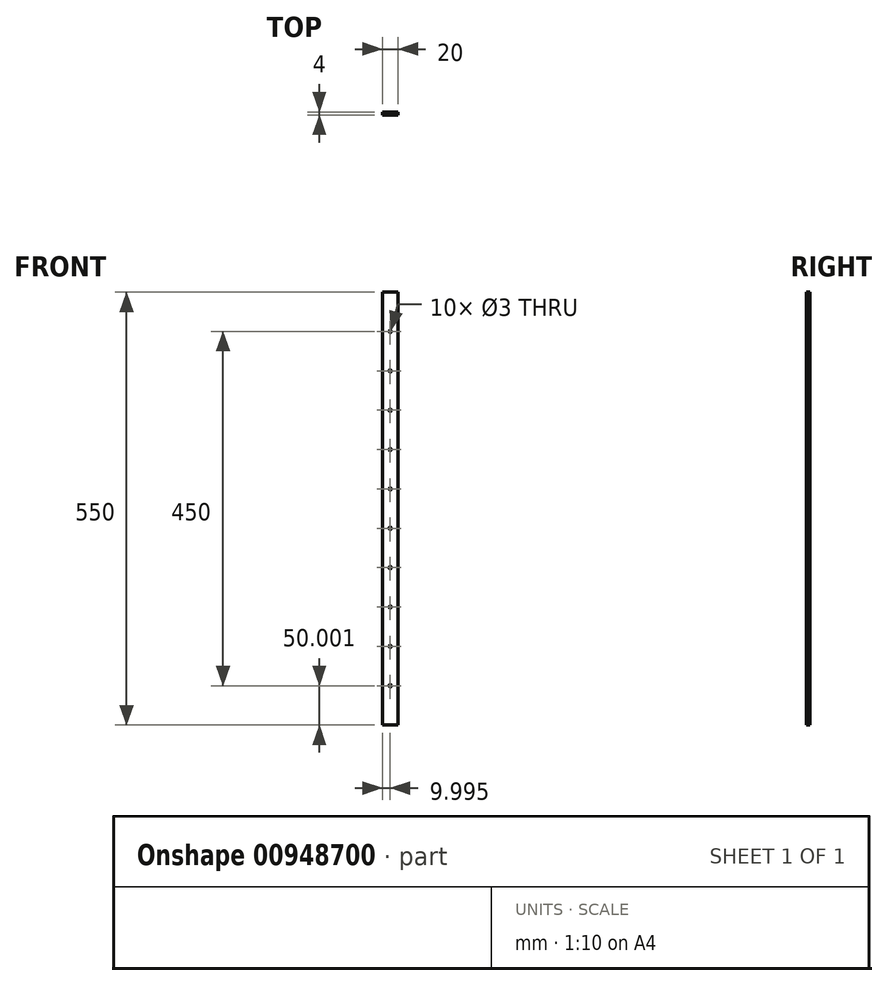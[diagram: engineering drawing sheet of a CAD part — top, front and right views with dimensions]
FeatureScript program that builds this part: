
annotation { "Feature Type Name" : "Feature", "Feature Type Description" : "" }
export const myFeature = defineFeature(function(context is Context, id is Id, definition is map)
    precondition{}
    {
        {
            var Q0;
            Q0=qCreatedBy(makeId("Front.planeOp"),FACE);
            var sketch = newSketch(context, id + "F0", { "sketchPlane" : qUnion([Q0])});
            skLineSegment(sketch, "E0.bottom", {"start": v(-67.64, 272.8) * mm, "end": v(-47.64, 272.8) * mm});
            skLineSegment(sketch, "E0.top", {"start": v(-67.64, -277.2) * mm, "end": v(-47.64, -277.2) * mm});
            skLineSegment(sketch, "E0.left", {"start": v(-67.64, 272.8) * mm, "end": v(-67.64, -277.2) * mm});
            skLineSegment(sketch, "E0.right", {"start": v(-47.64, 272.8) * mm, "end": v(-47.64, -277.2) * mm});
            skSolve(sketch);
        }
        {
            var Q0;
            Q0 = qSketchRegion(id + "F0", true);
            extrude(context, id + "F1", {"entities" : qUnion([Q0]), "depth" : 4 * mm, "offsetDistance" : 25 * mm});
        }
        {
            var Q0;
            Q0=makeQuery(id+"F1.opExtrude","CAP_FACE",FACE,{"disambiguationData":[OSD([sQuery(id+"F0.wireOp",EDGE,"E0.bottom"),sQuery(id+"F0.wireOp",EDGE,"E0.top"),sQuery(id+"F0.wireOp",EDGE,"E0.left"),sQuery(id+"F0.wireOp",EDGE,"E0.right")])],"isStart":false});
            var sketch = newSketch(context, id + "F2", { "sketchPlane" : qUnion([Q0])});
            skCircle(sketch, "E1", {"center": v(-57.64, 222.8) * mm, "radius": 1.5 * mm});
            skCircle(sketch, "E2.0.1.0", {"center": v(-57.64, 172.8) * mm, "radius": 1.5 * mm});
            skCircle(sketch, "E2.0.2.0", {"center": v(-57.64, 122.8) * mm, "radius": 1.5 * mm});
            skCircle(sketch, "E2.0.3.0", {"center": v(-57.64, 72.8) * mm, "radius": 1.5 * mm});
            skCircle(sketch, "E2.0.4.0", {"center": v(-57.64, 22.8) * mm, "radius": 1.5 * mm});
            skCircle(sketch, "E2.0.5.0", {"center": v(-57.64, -27.2) * mm, "radius": 1.5 * mm});
            skCircle(sketch, "E2.0.6.0", {"center": v(-57.64, -77.2) * mm, "radius": 1.5 * mm});
            skCircle(sketch, "E2.0.7.0", {"center": v(-57.64, -127.2) * mm, "radius": 1.5 * mm});
            skCircle(sketch, "E2.0.8.0", {"center": v(-57.64, -177.2) * mm, "radius": 1.5 * mm});
            skCircle(sketch, "E2.0.9.0", {"center": v(-57.64, -227.2) * mm, "radius": 1.5 * mm});
            skCircle(sketch, "E2.1.0.0", {"center": v(-32.64, 222.8) * mm, "radius": 1.5 * mm});
            skCircle(sketch, "E2.1.1.0", {"center": v(-32.64, 172.8) * mm, "radius": 1.5 * mm});
            skCircle(sketch, "E2.1.2.0", {"center": v(-32.64, 122.8) * mm, "radius": 1.5 * mm});
            skCircle(sketch, "E2.1.3.0", {"center": v(-32.64, 72.8) * mm, "radius": 1.5 * mm});
            skCircle(sketch, "E2.1.4.0", {"center": v(-32.64, 22.8) * mm, "radius": 1.5 * mm});
            skCircle(sketch, "E2.1.5.0", {"center": v(-32.64, -27.2) * mm, "radius": 1.5 * mm});
            skCircle(sketch, "E2.1.6.0", {"center": v(-32.64, -77.2) * mm, "radius": 1.5 * mm});
            skCircle(sketch, "E2.1.7.0", {"center": v(-32.64, -127.2) * mm, "radius": 1.5 * mm});
            skCircle(sketch, "E2.1.8.0", {"center": v(-32.64, -177.2) * mm, "radius": 1.5 * mm});
            skCircle(sketch, "E2.1.9.0", {"center": v(-32.64, -227.2) * mm, "radius": 1.5 * mm});
            skCircle(sketch, "E2.2.0.0", {"center": v(-7.64, 222.8) * mm, "radius": 1.5 * mm});
            skCircle(sketch, "E2.2.1.0", {"center": v(-7.64, 172.8) * mm, "radius": 1.5 * mm});
            skCircle(sketch, "E2.2.2.0", {"center": v(-7.64, 122.8) * mm, "radius": 1.5 * mm});
            skCircle(sketch, "E2.2.3.0", {"center": v(-7.64, 72.8) * mm, "radius": 1.5 * mm});
            skCircle(sketch, "E2.2.4.0", {"center": v(-7.64, 22.8) * mm, "radius": 1.5 * mm});
            skCircle(sketch, "E2.2.5.0", {"center": v(-7.64, -27.2) * mm, "radius": 1.5 * mm});
            skCircle(sketch, "E2.2.6.0", {"center": v(-7.64, -77.2) * mm, "radius": 1.5 * mm});
            skCircle(sketch, "E2.2.7.0", {"center": v(-7.64, -127.2) * mm, "radius": 1.5 * mm});
            skCircle(sketch, "E2.2.8.0", {"center": v(-7.64, -177.2) * mm, "radius": 1.5 * mm});
            skCircle(sketch, "E2.2.9.0", {"center": v(-7.64, -227.2) * mm, "radius": 1.5 * mm});
            skLineSegment(sketch, "E2.direction1", {"start": v(-57.64, 222.8) * mm, "end": v(-32.64, 222.8) * mm, "construction": true});
            skLineSegment(sketch, "E2.direction2", {"start": v(-57.64, 222.8) * mm, "end": v(-57.64, 172.8) * mm, "construction": true});
            skSolve(sketch);
        }
        {
            var Q0;
            Q0=makeQuery(id+"F2.imprint","IMPRINT",FACE,{"disambiguationData":[TD([[makeQuery(id+"F2.imprint","IMPRINT",EDGE,{"derivedFrom":sQuery(id+"F2.wireOp",EDGE,"E2.1.1.0")}),1.0]])]});
            var Q1;
            Q1=makeQuery(id+"F2.imprint","IMPRINT",FACE,{"disambiguationData":[TD([[makeQuery(id+"F2.imprint","IMPRINT",EDGE,{"derivedFrom":sQuery(id+"F2.wireOp",EDGE,"E2.1.2.0")}),1.0]])]});
            var Q2;
            Q2=makeQuery(id+"F2.imprint","IMPRINT",FACE,{"disambiguationData":[TD([[makeQuery(id+"F2.imprint","IMPRINT",EDGE,{"derivedFrom":sQuery(id+"F2.wireOp",EDGE,"E2.0.2.0")}),1.0]])]});
            var Q3;
            Q3=makeQuery(id+"F2.imprint","IMPRINT",FACE,{"disambiguationData":[TD([[makeQuery(id+"F2.imprint","IMPRINT",EDGE,{"derivedFrom":sQuery(id+"F2.wireOp",EDGE,"E2.2.0.0")}),1.0]])]});
            var Q4;
            Q4=makeQuery(id+"F2.imprint","IMPRINT",FACE,{"disambiguationData":[TD([[makeQuery(id+"F2.imprint","IMPRINT",EDGE,{"derivedFrom":sQuery(id+"F2.wireOp",EDGE,"E2.2.1.0")}),1.0]])]});
            var Q5;
            Q5=makeQuery(id+"F2.imprint","IMPRINT",FACE,{"disambiguationData":[TD([[makeQuery(id+"F2.imprint","IMPRINT",EDGE,{"derivedFrom":sQuery(id+"F2.wireOp",EDGE,"E2.2.2.0")}),1.0]])]});
            var Q6;
            Q6=makeQuery(id+"F2.imprint","IMPRINT",FACE,{"disambiguationData":[TD([[makeQuery(id+"F2.imprint","IMPRINT",EDGE,{"derivedFrom":sQuery(id+"F2.wireOp",EDGE,"E2.0.1.0")}),1.0]])]});
            var Q7;
            Q7=makeQuery(id+"F2.imprint","IMPRINT",FACE,{"disambiguationData":[TD([[makeQuery(id+"F2.imprint","IMPRINT",EDGE,{"derivedFrom":sQuery(id+"F2.wireOp",EDGE,"E2.1.0.0")}),1.0]])]});
            var Q8;
            Q8=makeQuery(id+"F2.imprint","IMPRINT",FACE,{"disambiguationData":[TD([[makeQuery(id+"F2.imprint","IMPRINT",EDGE,{"derivedFrom":sQuery(id+"F2.wireOp",EDGE,"E1")}),1.0]])]});
            var Q9;
            Q9=makeQuery(id+"F2.imprint","IMPRINT",FACE,{"disambiguationData":[TD([[makeQuery(id+"F2.imprint","IMPRINT",EDGE,{"derivedFrom":sQuery(id+"F2.wireOp",EDGE,"E2.0.5.0")}),1.0]])]});
            var Q10;
            Q10=makeQuery(id+"F2.imprint","IMPRINT",FACE,{"disambiguationData":[TD([[makeQuery(id+"F2.imprint","IMPRINT",EDGE,{"derivedFrom":sQuery(id+"F2.wireOp",EDGE,"E2.1.6.0")}),1.0]])]});
            var Q11;
            Q11=makeQuery(id+"F2.imprint","IMPRINT",FACE,{"disambiguationData":[TD([[makeQuery(id+"F2.imprint","IMPRINT",EDGE,{"derivedFrom":sQuery(id+"F2.wireOp",EDGE,"E2.0.7.0")}),1.0]])]});
            var Q12;
            Q12=makeQuery(id+"F2.imprint","IMPRINT",FACE,{"disambiguationData":[TD([[makeQuery(id+"F2.imprint","IMPRINT",EDGE,{"derivedFrom":sQuery(id+"F2.wireOp",EDGE,"E2.0.6.0")}),1.0]])]});
            var Q13;
            Q13=makeQuery(id+"F2.imprint","IMPRINT",FACE,{"disambiguationData":[TD([[makeQuery(id+"F2.imprint","IMPRINT",EDGE,{"derivedFrom":sQuery(id+"F2.wireOp",EDGE,"E2.0.9.0")}),1.0]])]});
            var Q14;
            Q14=makeQuery(id+"F2.imprint","IMPRINT",FACE,{"disambiguationData":[TD([[makeQuery(id+"F2.imprint","IMPRINT",EDGE,{"derivedFrom":sQuery(id+"F2.wireOp",EDGE,"E2.0.3.0")}),1.0]])]});
            var Q15;
            Q15=makeQuery(id+"F2.imprint","IMPRINT",FACE,{"disambiguationData":[TD([[makeQuery(id+"F2.imprint","IMPRINT",EDGE,{"derivedFrom":sQuery(id+"F2.wireOp",EDGE,"E2.0.4.0")}),1.0]])]});
            var Q16;
            Q16=makeQuery(id+"F2.imprint","IMPRINT",FACE,{"disambiguationData":[TD([[makeQuery(id+"F2.imprint","IMPRINT",EDGE,{"derivedFrom":sQuery(id+"F2.wireOp",EDGE,"E2.0.8.0")}),1.0]])]});
            var Q17;
            Q17=makeQuery(id+"F2.imprint","IMPRINT",FACE,{"disambiguationData":[TD([[makeQuery(id+"F2.imprint","IMPRINT",EDGE,{"derivedFrom":sQuery(id+"F2.wireOp",EDGE,"E2.1.5.0")}),1.0]])]});
            var Q18;
            Q18=makeQuery(id+"F2.imprint","IMPRINT",FACE,{"disambiguationData":[TD([[makeQuery(id+"F2.imprint","IMPRINT",EDGE,{"derivedFrom":sQuery(id+"F2.wireOp",EDGE,"E2.1.3.0")}),1.0]])]});
            var Q19;
            Q19=makeQuery(id+"F2.imprint","IMPRINT",FACE,{"disambiguationData":[TD([[makeQuery(id+"F2.imprint","IMPRINT",EDGE,{"derivedFrom":sQuery(id+"F2.wireOp",EDGE,"E2.1.4.0")}),1.0]])]});
            var Q20;
            Q20=makeQuery(id+"F2.imprint","IMPRINT",FACE,{"disambiguationData":[TD([[makeQuery(id+"F2.imprint","IMPRINT",EDGE,{"derivedFrom":sQuery(id+"F2.wireOp",EDGE,"E2.1.7.0")}),1.0]])]});
            var Q21;
            Q21=makeQuery(id+"F2.imprint","IMPRINT",FACE,{"disambiguationData":[TD([[makeQuery(id+"F2.imprint","IMPRINT",EDGE,{"derivedFrom":sQuery(id+"F2.wireOp",EDGE,"E2.2.9.0")}),1.0]])]});
            var Q22;
            Q22=makeQuery(id+"F2.imprint","IMPRINT",FACE,{"disambiguationData":[TD([[makeQuery(id+"F2.imprint","IMPRINT",EDGE,{"derivedFrom":sQuery(id+"F2.wireOp",EDGE,"E2.1.8.0")}),1.0]])]});
            var Q23;
            Q23=makeQuery(id+"F2.imprint","IMPRINT",FACE,{"disambiguationData":[TD([[makeQuery(id+"F2.imprint","IMPRINT",EDGE,{"derivedFrom":sQuery(id+"F2.wireOp",EDGE,"E2.2.8.0")}),1.0]])]});
            var Q24;
            Q24=makeQuery(id+"F2.imprint","IMPRINT",FACE,{"disambiguationData":[TD([[makeQuery(id+"F2.imprint","IMPRINT",EDGE,{"derivedFrom":sQuery(id+"F2.wireOp",EDGE,"E2.1.9.0")}),1.0]])]});
            var Q25;
            Q25=makeQuery(id+"F2.imprint","IMPRINT",FACE,{"disambiguationData":[TD([[makeQuery(id+"F2.imprint","IMPRINT",EDGE,{"derivedFrom":sQuery(id+"F2.wireOp",EDGE,"E2.2.7.0")}),1.0]])]});
            var Q26;
            Q26=makeQuery(id+"F2.imprint","IMPRINT",FACE,{"disambiguationData":[TD([[makeQuery(id+"F2.imprint","IMPRINT",EDGE,{"derivedFrom":sQuery(id+"F2.wireOp",EDGE,"E2.2.6.0")}),1.0]])]});
            var Q27;
            Q27=makeQuery(id+"F2.imprint","IMPRINT",FACE,{"disambiguationData":[TD([[makeQuery(id+"F2.imprint","IMPRINT",EDGE,{"derivedFrom":sQuery(id+"F2.wireOp",EDGE,"E2.2.5.0")}),1.0]])]});
            var Q28;
            Q28=makeQuery(id+"F2.imprint","IMPRINT",FACE,{"disambiguationData":[TD([[makeQuery(id+"F2.imprint","IMPRINT",EDGE,{"derivedFrom":sQuery(id+"F2.wireOp",EDGE,"E2.2.4.0")}),1.0]])]});
            var Q29;
            Q29=makeQuery(id+"F2.imprint","IMPRINT",FACE,{"disambiguationData":[TD([[makeQuery(id+"F2.imprint","IMPRINT",EDGE,{"derivedFrom":sQuery(id+"F2.wireOp",EDGE,"E2.2.3.0")}),1.0]])]});
            extrude(context, id + "F3", {"entities" : qUnion([Q0, Q1, Q2, Q3, Q4, Q5, Q6, Q7, Q8, Q9, Q10, Q11, Q12, Q13, Q14, Q15, Q16, Q17, Q18, Q19, Q20, Q21, Q22, Q23, Q24, Q25, Q26, Q27, Q28, Q29]), "operationType" : NewBodyOperationType.REMOVE, "oppositeDirection" : true, "depth" : 25 * mm, "offsetDistance" : 25 * mm});
        }
    });
